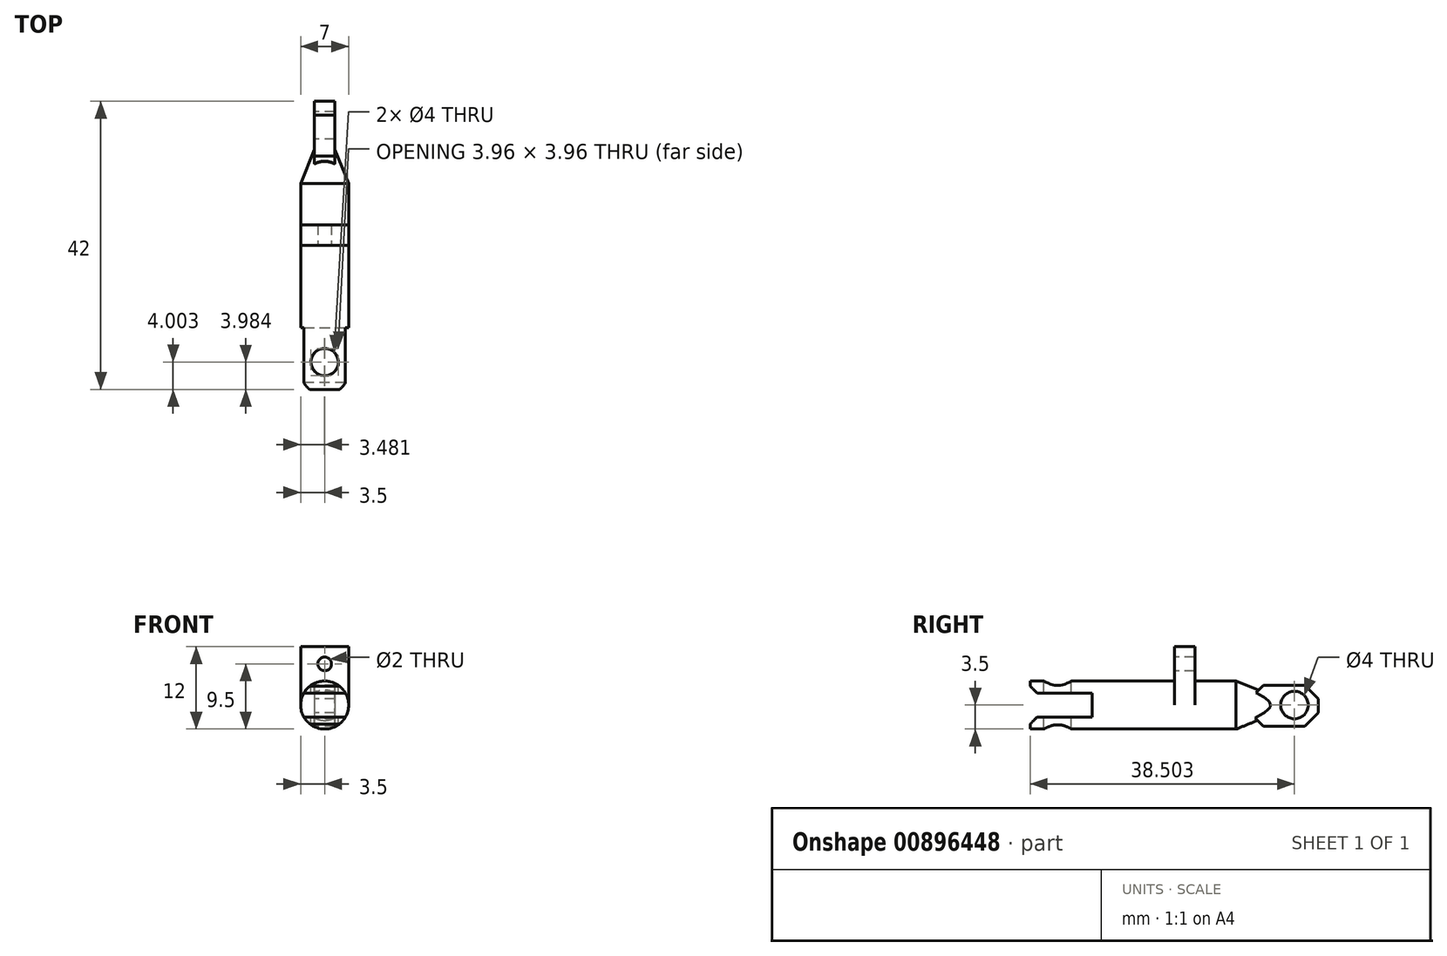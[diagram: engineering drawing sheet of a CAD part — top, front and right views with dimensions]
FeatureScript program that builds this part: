
annotation { "Feature Type Name" : "Feature", "Feature Type Description" : "" }
export const myFeature = defineFeature(function(context is Context, id is Id, definition is map)
    precondition{}
    {
        {
            var Q0;
            Q0=qCreatedBy(makeId("Right.planeOp"),FACE);
            var sketch = newSketch(context, id + "F0", { "sketchPlane" : qUnion([Q0])});
            skLineSegment(sketch, "E0", {"start": v(16.86, 0.9) * mm, "end": v(16.86, -1.1) * mm});
            skLineSegment(sketch, "E1", {"start": v(16.86, -1.1) * mm, "end": v(14.86, -3.1) * mm});
            skLineSegment(sketch, "E2", {"start": v(14.86, -3.1) * mm, "end": v(8.86, -3.1) * mm});
            skLineSegment(sketch, "E3", {"start": v(8.86, -3.1) * mm, "end": v(6.86, -1.1) * mm});
            skLineSegment(sketch, "E4", {"start": v(6.86, -1.1) * mm, "end": v(6.86, 0.9) * mm});
            skLineSegment(sketch, "E5", {"start": v(6.86, 0.9) * mm, "end": v(8.86, 2.9) * mm});
            skLineSegment(sketch, "E6", {"start": v(8.86, 2.9) * mm, "end": v(14.86, 2.9) * mm});
            skLineSegment(sketch, "E7", {"start": v(14.86, 2.9) * mm, "end": v(16.86, 0.9) * mm});
            skSolve(sketch);
        }
        {
            var Q0;
            Q0 = qSketchRegion(id + "F0", true);
            extrude(context, id + "F1", {"entities" : qUnion([Q0]), "endBound" : BoundingType.SYMMETRIC, "depth" : 3 * mm, "offsetDistance" : 25 * mm});
        }
        {
            var Q0;
            Q0=makeQuery(id+"F1.opExtrude","CAP_FACE",FACE,{"disambiguationData":[OSD([sQuery(id+"F0.wireOp",EDGE,"E0"),sQuery(id+"F0.wireOp",EDGE,"E1"),sQuery(id+"F0.wireOp",EDGE,"E2"),sQuery(id+"F0.wireOp",EDGE,"E3"),sQuery(id+"F0.wireOp",EDGE,"E4"),sQuery(id+"F0.wireOp",EDGE,"E5"),sQuery(id+"F0.wireOp",EDGE,"E6"),sQuery(id+"F0.wireOp",EDGE,"E7")])],"isStart":true});
            var sketch = newSketch(context, id + "F2", { "sketchPlane" : qUnion([Q0])});
            skCircle(sketch, "E8", {"center": v(-13.36, 0) * mm, "radius": 2 * mm});
            skSolve(sketch);
        }
        {
            var Q0;
            Q0 = qSketchRegion(id + "F2", true);
            extrude(context, id + "F3", {"entities" : qUnion([Q0]), "operationType" : NewBodyOperationType.REMOVE, "endBound" : BoundingType.THROUGH_ALL, "oppositeDirection" : true, "depth" : 25 * mm, "offsetDistance" : 25 * mm});
        }
        {
            var Q0;
            Q0=qCreatedBy(makeId("Top.planeOp"),FACE);
            var sketch = newSketch(context, id + "F4", { "sketchPlane" : qUnion([Q0])});
            skLineSegment(sketch, "E9", {"start": v(0, 9.86) * mm, "end": v(-1.5, 9.86) * mm});
            skLineSegment(sketch, "E10", {"start": v(-1.5, 9.86) * mm, "end": v(-3.5, 4.86) * mm});
            skLineSegment(sketch, "E11", {"start": v(-3.5, 4.86) * mm, "end": v(0, 4.86) * mm});
            skLineSegment(sketch, "E12", {"start": v(0, 4.86) * mm, "end": v(0, 9.86) * mm});
            skSolve(sketch);
        }
        {
            var Q0;
            Q0 = qSketchRegion(id + "F4", true);
            var Q1;
            Q1=sQuery(id+"F4.wireOp",EDGE,"E12");
            revolve(context, id + "F5", {"operationType" : NewBodyOperationType.ADD, "surfaceOperationType" : NewSurfaceOperationType.NEW, "entities" : qUnion([Q0]), "axis" : qUnion([Q1]), "revolveType" : RevolveType.FULL});
        }
        {
            var Q0;
            Q0=makeQuery(id+"F5.opRevolve","SWEPT_FACE",FACE,{"disambiguationData":[OSD([sQuery(id+"F4.wireOp",EDGE,"E11")])]});
            extrude(context, id + "F6", {"entities" : qUnion([Q0]), "operationType" : NewBodyOperationType.ADD, "depth" : 30 * mm, "offsetDistance" : 25 * mm});
        }
        {
            var Q0;
            Q0=qCreatedBy(makeId("Right.planeOp"),FACE);
            var sketch = newSketch(context, id + "F7", { "sketchPlane" : qUnion([Q0])});
            skLineSegment(sketch, "E13.bottom", {"start": v(-31.06, 1.75) * mm, "end": v(-16.14, 1.75) * mm});
            skLineSegment(sketch, "E13.top", {"start": v(-31.06, -1.75) * mm, "end": v(-16.14, -1.75) * mm});
            skLineSegment(sketch, "E13.left", {"start": v(-31.06, 1.75) * mm, "end": v(-31.06, -1.75) * mm});
            skLineSegment(sketch, "E13.right", {"start": v(-16.14, 1.75) * mm, "end": v(-16.14, -1.75) * mm});
            skSolve(sketch);
        }
        {
            var Q0;
            Q0 = qSketchRegion(id + "F7", true);
            extrude(context, id + "F8", {"entities" : qUnion([Q0]), "operationType" : NewBodyOperationType.REMOVE, "endBound" : BoundingType.SYMMETRIC, "oppositeDirection" : true, "depth" : 25 * mm, "offsetDistance" : 25 * mm});
        }
        {
            var Q0;
            Q0=qCreatedBy(makeId("Top.planeOp"),FACE);
            var sketch = newSketch(context, id + "F9", { "sketchPlane" : qUnion([Q0])});
            skLineSegment(sketch, "E14.bottom", {"start": v(-3.5, -1.14) * mm, "end": v(3.5, -1.14) * mm});
            skLineSegment(sketch, "E14.top", {"start": v(-3.5, -4.14) * mm, "end": v(3.5, -4.14) * mm});
            skLineSegment(sketch, "E14.left", {"start": v(-3.5, -1.14) * mm, "end": v(-3.5, -4.14) * mm});
            skLineSegment(sketch, "E14.right", {"start": v(3.5, -1.14) * mm, "end": v(3.5, -4.14) * mm});
            skSolve(sketch);
        }
        {
            var Q0;
            Q0 = qSketchRegion(id + "F9", true);
            extrude(context, id + "F10", {"entities" : qUnion([Q0]), "operationType" : NewBodyOperationType.ADD, "depth" : 8.5 * mm, "offsetDistance" : 25 * mm});
        }
        {
            var Q0;
            Q0=qCreatedBy(makeId("Top.planeOp"),FACE);
            var sketch = newSketch(context, id + "F11", { "sketchPlane" : qUnion([Q0])});
            skCircle(sketch, "E15", {"center": v(0, -21.14) * mm, "radius": 2 * mm});
            skSolve(sketch);
        }
        {
            var Q0;
            Q0=makeQuery(id+"F11.imprint","IMPRINT",FACE,{"disambiguationData":[TD([[makeQuery(id+"F11.imprint","IMPRINT",EDGE,{"derivedFrom":sQuery(id+"F11.wireOp",EDGE,"E15")}),1.0]])]});
            extrude(context, id + "F12", {"entities" : qUnion([Q0]), "operationType" : NewBodyOperationType.REMOVE, "endBound" : BoundingType.SYMMETRIC, "oppositeDirection" : true, "depth" : 25 * mm, "offsetDistance" : 25 * mm});
        }
        {
            var Q0;
            Q0=makeQuery(id+"F10.opExtrude","SWEPT_FACE",FACE,{"disambiguationData":[OSD([sQuery(id+"F9.wireOp",EDGE,"E14.top")])]});
            var sketch = newSketch(context, id + "F13", { "sketchPlane" : qUnion([Q0])});
            skCircle(sketch, "E16", {"center": v(0, 6) * mm, "radius": 1 * mm});
            skSolve(sketch);
        }
        {
            var Q0;
            Q0=makeQuery(id+"F13.imprint","IMPRINT",FACE,{"disambiguationData":[TD([[makeQuery(id+"F13.imprint","IMPRINT",EDGE,{"derivedFrom":sQuery(id+"F13.wireOp",EDGE,"E16")}),1.0]])]});
            extrude(context, id + "F14", {"entities" : qUnion([Q0]), "operationType" : NewBodyOperationType.REMOVE, "endBound" : BoundingType.THROUGH_ALL, "oppositeDirection" : true, "depth" : 25 * mm, "offsetDistance" : 25 * mm});
        }
        {
            var Q0;
            Q0=makeQuery(id+"F8.boolean.opBoolean","INTERSECT",EDGE,{"derivedFrom":[makeQuery(id+"F6.opExtrude","CAP_FACE",FACE,{"disambiguationData":[OSD([sQuery(id+"F4.wireOp",EDGE,"E11")])],"isStart":false}),makeQuery(id+"F8.opExtrude","SWEPT_FACE",FACE,{"disambiguationData":[OSD([sQuery(id+"F7.wireOp",EDGE,"E13.top")])]})]});
            var Q1;
            Q1=makeQuery(id+"F8.boolean.opBoolean","INTERSECT",EDGE,{"derivedFrom":[makeQuery(id+"F6.opExtrude","CAP_FACE",FACE,{"disambiguationData":[OSD([sQuery(id+"F4.wireOp",EDGE,"E11")])],"isStart":false}),makeQuery(id+"F8.opExtrude","SWEPT_FACE",FACE,{"disambiguationData":[OSD([sQuery(id+"F7.wireOp",EDGE,"E13.bottom")])]})]});
            chamfer(context, id + "F15", {"entities" : qUnion([Q0, Q1]), "width" : 1 * mm, "tangentPropagation" : true});
        }
    });
